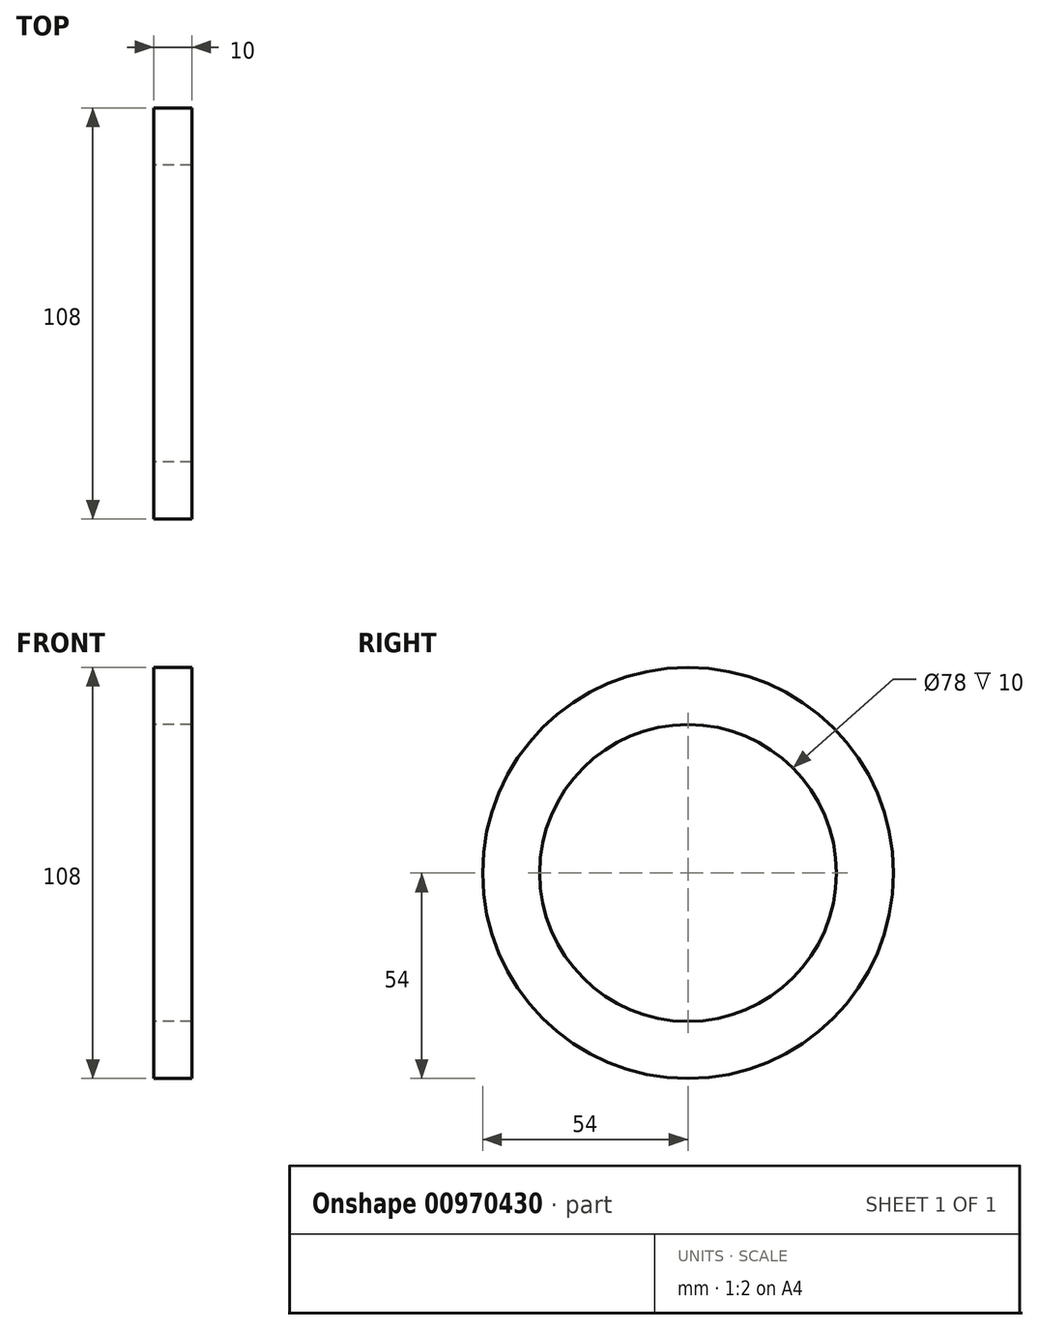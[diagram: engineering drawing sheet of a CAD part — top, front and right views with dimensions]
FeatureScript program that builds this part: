
annotation { "Feature Type Name" : "Feature", "Feature Type Description" : "" }
export const myFeature = defineFeature(function(context is Context, id is Id, definition is map)
    precondition{}
    {
        {
            var Q0;
            Q0=qCreatedBy(makeId("Right.planeOp"),FACE);
            var sketch = newSketch(context, id + "F0", { "sketchPlane" : qUnion([Q0])});
            skCircle(sketch, "E0", {"center": v(0, 0) * mm, "radius": 46.5 * mm, "construction": true});
            skCircle(sketch, "E1.0", {"center": v(0, 0) * mm, "radius": 54 * mm});
            skCircle(sketch, "E2.0", {"center": v(0, 0) * mm, "radius": 39 * mm});
            skSolve(sketch);
        }
        {
            var Q0;
            Q0=makeQuery(id+"F0.imprint","IMPRINT",FACE,{"disambiguationData":[TD([[makeQuery(id+"F0.imprint","IMPRINT",EDGE,{"derivedFrom":sQuery(id+"F0.wireOp",EDGE,"E1.0")}),1.0]])]});
            extrude(context, id + "F1", {"entities" : qUnion([Q0]), "depth" : 10 * mm, "offsetDistance" : 25 * mm});
        }
    });
